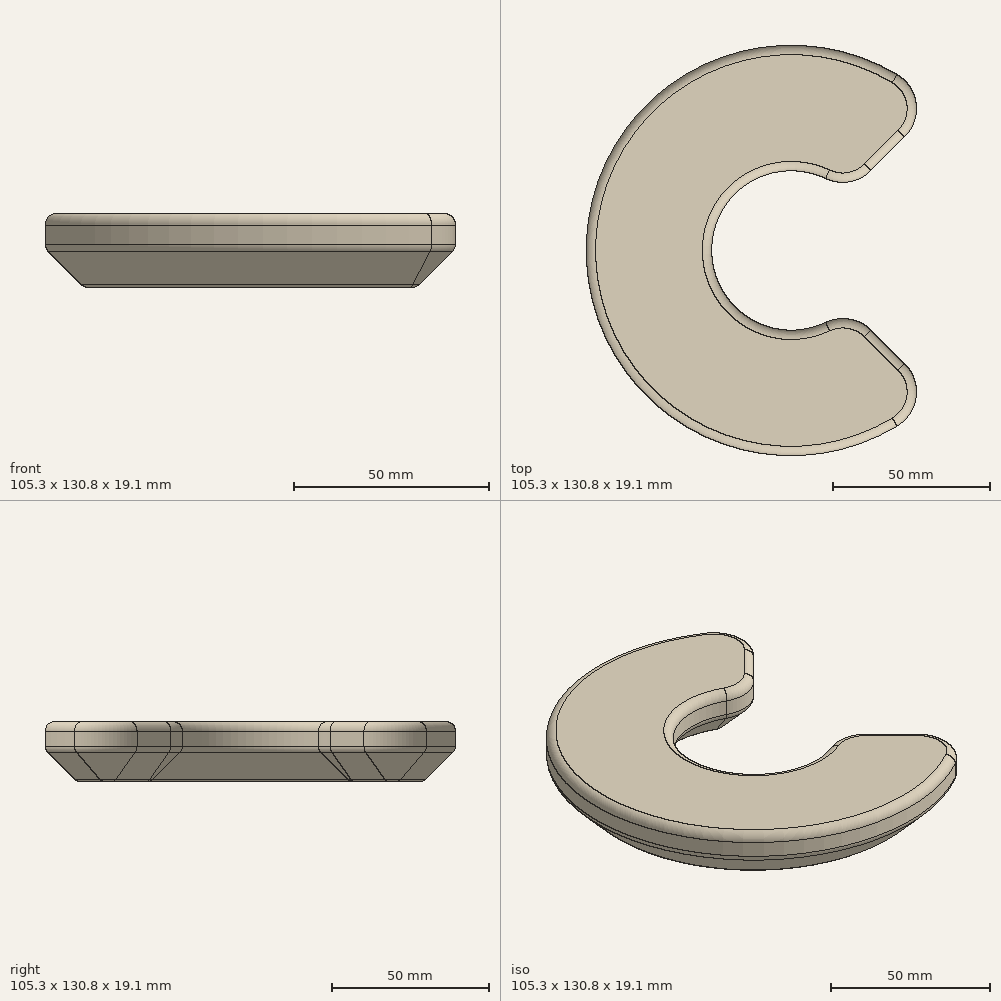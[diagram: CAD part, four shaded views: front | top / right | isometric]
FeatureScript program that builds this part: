
annotation { "Feature Type Name" : "Feature", "Feature Type Description" : "" }
export const myFeature = defineFeature(function(context is Context, id is Id, definition is map)
    precondition{}
    {
        {
            var Q0;
            Q0=qCreatedBy(makeId("Front.planeOp"),FACE);
            var sketch = newSketch(context, id + "F0", { "sketchPlane" : qUnion([Q0])});
            skLineSegment(sketch, "E0.bottom", {"start": v(0, 0) * mm, "end": v(-40, 0) * mm});
            skLineSegment(sketch, "E0.top", {"start": v(0, 19.05) * mm, "end": v(-40, 19.05) * mm});
            skLineSegment(sketch, "E0.left", {"start": v(0, 0) * mm, "end": v(0, 19.05) * mm});
            skLineSegment(sketch, "E0.right", {"start": v(-40, 0) * mm, "end": v(-40, 19.05) * mm});
            skLineSegment(sketch, "E1", {"start": v(25.4, 0) * mm, "end": v(25.4, 19.05) * mm});
            skSolve(sketch);
        }
        {
            var Q0;
            Q0=makeQuery(id+"F0.imprint","IMPRINT",FACE,{"disambiguationData":[TD([[makeQuery(id+"F0.imprint","IMPRINT",EDGE,{"derivedFrom":sQuery(id+"F0.wireOp",EDGE,"E0.bottom")}),-1.0]])]});
            var Q1;
            Q1=sQuery(id+"F0.wireOp",EDGE,"E1");
            revolve(context, id + "F1", {"entities" : qUnion([Q0]), "axis" : qUnion([Q1]), "revolveType" : RevolveType.SYMMETRIC, "angle" : 270 * degree});
        }
        {
            var Q0;
            Q0=makeQuery(id+"F1.opRevolve","SWEPT_EDGE",EDGE,{"disambiguationData":[OSD([sQuery(id+"F0.wireOp",EDGE,"E0.top"),sQuery(id+"F0.wireOp",EDGE,"E0.left")])]});
            var Q1;
            Q1=makeQuery(id+"F1.opRevolve","SWEPT_EDGE",EDGE,{"disambiguationData":[OSD([sQuery(id+"F0.wireOp",EDGE,"E0.top"),sQuery(id+"F0.wireOp",EDGE,"E0.right")])]});
            var Q2;
            Q2=makeQuery(id+"F1.opRevolve","CAP_EDGE",EDGE,{"disambiguationData":[OSD([sQuery(id+"F0.wireOp",EDGE,"E0.top")])],"isStart":true});
            var Q3;
            Q3=makeQuery(id+"F1.opRevolve","CAP_EDGE",EDGE,{"disambiguationData":[OSD([sQuery(id+"F0.wireOp",EDGE,"E0.top")])],"isStart":false});
            fillet(context, id + "F2", {"entities" : qUnion([Q0, Q1, Q2, Q3]), "radius" : 3 * mm, "tangentPropagation" : true, "allowEdgeOverflow" : false});
        }
        {
            var Q0;
            Q0=makeQuery(id+"F1.opRevolve","CAP_EDGE",EDGE,{"disambiguationData":[OSD([sQuery(id+"F0.wireOp",EDGE,"E0.right")])],"isStart":false});
            var Q1;
            Q1=makeQuery(id+"F1.opRevolve","CAP_EDGE",EDGE,{"disambiguationData":[OSD([sQuery(id+"F0.wireOp",EDGE,"E0.left")])],"isStart":false});
            var Q2;
            Q2=makeQuery(id+"F1.opRevolve","CAP_EDGE",EDGE,{"disambiguationData":[OSD([sQuery(id+"F0.wireOp",EDGE,"E0.left")])],"isStart":true});
            var Q3;
            Q3=makeQuery(id+"F1.opRevolve","CAP_EDGE",EDGE,{"disambiguationData":[OSD([sQuery(id+"F0.wireOp",EDGE,"E0.right")])],"isStart":true});
            fillet(context, id + "F3", {"entities" : qUnion([Q0, Q1, Q2, Q3]), "radius" : 12.7 * mm, "tangentPropagation" : true, "allowEdgeOverflow" : false});
        }
        {
            var Q0;
            Q0=makeQuery(id+"F1.opRevolve","CAP_EDGE",EDGE,{"disambiguationData":[OSD([sQuery(id+"F0.wireOp",EDGE,"E0.bottom")])],"isStart":false});
            var Q1;
            Q1=makeQuery(id+"F1.opRevolve","CAP_EDGE",EDGE,{"disambiguationData":[OSD([sQuery(id+"F0.wireOp",EDGE,"E0.bottom")])],"isStart":true});
            var Q2;
            Q2=makeQuery(id+"F1.opRevolve","SWEPT_EDGE",EDGE,{"disambiguationData":[OSD([sQuery(id+"F0.wireOp",EDGE,"E0.bottom"),sQuery(id+"F0.wireOp",EDGE,"E0.left")])]});
            var Q3;
            Q3=makeQuery(id+"F1.opRevolve","SWEPT_EDGE",EDGE,{"disambiguationData":[OSD([sQuery(id+"F0.wireOp",EDGE,"E0.bottom"),sQuery(id+"F0.wireOp",EDGE,"E0.right")])]});
            chamfer(context, id + "F4", {"entities" : qUnion([Q0, Q1, Q2, Q3]), "width" : 10 * mm, "tangentPropagation" : true});
        }
        {
            var Q0;
            {var subQ0=sQuery(id+"F0.wireOp",EDGE,"E0.bottom");Q0=makeQuery(id+"F4.opChamfer","BLEND_EDGE",EDGE,{"blendedFrom":[makeQuery(id+"F1.opRevolve","SWEPT_EDGE",EDGE,{"disambiguationData":[OSD([subQ0,sQuery(id+"F0.wireOp",EDGE,"E0.right")])]}),makeQuery(id+"F1.opRevolve","SWEPT_FACE",FACE,{"disambiguationData":[OSD([subQ0])]})],"blendedInto":[makeQuery(id+"F1.opRevolve","SWEPT_FACE",FACE,{"disambiguationData":[OSD([subQ0])]})]});}
            var Q1;
            {var subQ0=sQuery(id+"F0.wireOp",EDGE,"E0.right");Q1=makeQuery(id+"F4.opChamfer","BLEND_EDGE",EDGE,{"blendedFrom":[makeQuery(id+"F1.opRevolve","SWEPT_EDGE",EDGE,{"disambiguationData":[OSD([sQuery(id+"F0.wireOp",EDGE,"E0.bottom"),subQ0])]}),makeQuery(id+"F1.opRevolve","SWEPT_FACE",FACE,{"disambiguationData":[OSD([subQ0])]})],"blendedInto":[makeQuery(id+"F1.opRevolve","SWEPT_FACE",FACE,{"disambiguationData":[OSD([subQ0])]})]});}
            fillet(context, id + "F5", {"entities" : qUnion([Q0, Q1]), "radius" : 2.54 * mm, "tangentPropagation" : true, "allowEdgeOverflow" : false});
        }
    });
